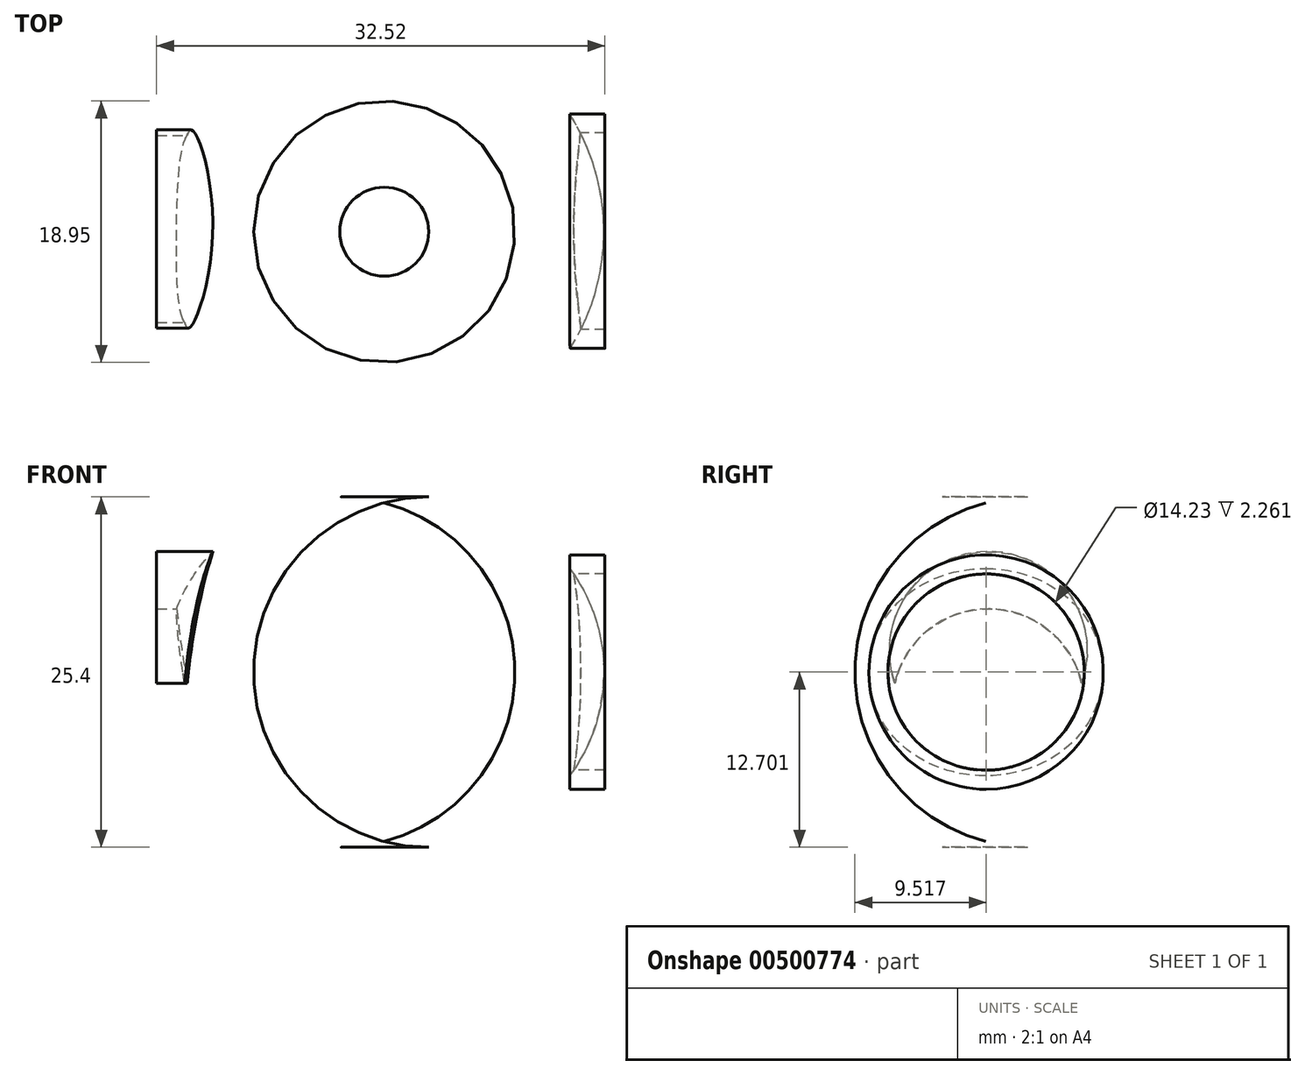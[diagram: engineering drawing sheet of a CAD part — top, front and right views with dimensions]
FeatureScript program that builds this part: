
annotation { "Feature Type Name" : "Feature", "Feature Type Description" : "" }
export const myFeature = defineFeature(function(context is Context, id is Id, definition is map)
    precondition{}
    {
        {
            var Q0;
            Q0=qCreatedBy(makeId("Top.planeOp"),FACE);
            var sketch = newSketch(context, id + "F0", { "sketchPlane" : qUnion([Q0])});
            skCircle(sketch, "E0", {"center": v(-45.47, 20) * mm, "radius": 15.93 * mm});
            skSolve(sketch);
        }
        {
            var Q0;
            Q0=makeQuery(id+"F0.imprint","IMPRINT",FACE,{"disambiguationData":[TD([[makeQuery(id+"F0.imprint","IMPRINT",EDGE,{"derivedFrom":sQuery(id+"F0.wireOp",EDGE,"E0")}),1.0]])]});
            extrude(context, id + "F1", {"entities" : qUnion([Q0]), "depth" : 25.4 * mm});
        }
        {
            var Q0;
            Q0=makeQuery(id+"F1.opExtrude","CAP_EDGE",EDGE,{"disambiguationData":[OSD([sQuery(id+"F0.wireOp",EDGE,"E0")])],"isStart":false});
            var Q1;
            Q1=makeQuery(id+"F1.opExtrude","CAP_EDGE",EDGE,{"disambiguationData":[OSD([sQuery(id+"F0.wireOp",EDGE,"E0")])],"isStart":true});
            fillet(context, id + "F2", {"entities" : qUnion([Q0, Q1]), "radius" : 12.7 * mm, "tangentPropagation" : true, "allowEdgeOverflow" : false});
        }
        {
            var Q0;
            Q0=qCreatedBy(makeId("Front.planeOp"),FACE);
            cPlane(context, id + "F3", {"entities" : qUnion([Q0]), "cplaneType" : CPlaneType.OFFSET, "offset" : 8.48 * mm, "oppositeDirection" : true, "width" : 152.4 * mm, "height" : 152.4 * mm});
        }
        {
            var Q0;
            Q0=qCreatedBy(id+"F3.planeOp",FACE);
            var sketch = newSketch(context, id + "F4", { "sketchPlane" : qUnion([Q0])});
            skCircle(sketch, "E1", {"center": v(-45.44, 12.7) * mm, "radius": 8 * mm});
            skFitSpline(sketch, "E2", {"points": [v(-42.57, 5.23) * mm, v(-44.89, 6.19) * mm, v(-47.41, 7.81) * mm, v(-49.76, 10.08) * mm, v(-50.28, 13.29) * mm, v(-49.38, 15.64) * mm, v(-47.11, 17.14) * mm, v(-44.37, 17.05) * mm, v(-42.02, 15.99) * mm, v(-41.12, 13.68) * mm, v(-41.85, 11.58) * mm, v(-44.29, 10.85) * mm, v(-46.64, 11.28) * mm, v(-47.5, 12.4) * mm, v(-47.33, 13.42) * mm, v(-45.44, 12.7) * mm, v(-44.07, 12.7) * mm, v(-42.75, 13.33) * mm, v(-42.88, 14.66) * mm, v(-43.52, 15.86) * mm, v(-45.1, 16.37) * mm, v(-47.2, 16.07) * mm, v(-48.65, 14.49) * mm, v(-49.04, 12.7) * mm, v(-48.44, 10.34) * mm, v(-46.55, 8.84) * mm, v(-44.16, 7.34) * mm, v(-41.85, 6.44) * mm, v(-40.86, 6.15) * mm, v(-42.57, 5.23) * mm]});
            skArc(sketch, "E3", {"start": v(-42.26, 6.54) * mm, "mid": v(-47.59, 19.27) * mm, "end": v(-44.4, 5.85) * mm});
            skPoint(sketch, "E4.17.internal.orphan", {"position": v(-45.56, 13.68) * mm});
            skPoint(sketch, "E4.19.internal.orphan", {"position": v(-45.44, 11.58) * mm});
            skPoint(sketch, "E4.21.internal.orphan", {"position": v(-43.51, 11.58) * mm});
            skPoint(sketch, "E4.24.internal.orphan", {"position": v(-42.87, 14.53) * mm});
            skFitSpline(sketch, "E5", {"points": [v(-47.1, 17.14) * mm, v(-45.98, 17.3) * mm, v(-44.76, 17.3) * mm, v(-43.5, 17.06) * mm, v(-42.6, 16.55) * mm, v(-41.92, 15.48) * mm, v(-41.67, 12.8) * mm, v(-42.25, 11.37) * mm, v(-42.91, 10.67) * mm, v(-44.73, 10.22) * mm, v(-45.97, 10.6) * mm, v(-46.64, 11.28) * mm, v(-47, 12.26) * mm, v(-46.88, 13.56) * mm, v(-46.14, 14.44) * mm, v(-45.69, 14.51) * mm, v(-45.4, 14.39) * mm, v(-45.56, 13.68) * mm, v(-45.81, 12.73) * mm, v(-45.44, 11.58) * mm, v(-44.41, 11.41) * mm, v(-43.51, 11.58) * mm, v(-43.04, 12.26) * mm, v(-42.75, 13.33) * mm, v(-42.87, 14.53) * mm, v(-42.87, 14.65) * mm, v(-43.51, 15.85) * mm, v(-45.1, 16.37) * mm, v(-46.09, 16.38) * mm, v(-47.2, 16.07) * mm, v(-47.1, 17.14) * mm]});
            skLineSegment(sketch, "E6", {"start": v(-45.98, 17.3) * mm, "end": v(-47.1, 17.14) * mm});
            skSolve(sketch);
        }
        {
            var Q0;
            Q0 = qSketchRegion(id + "F4", true);
            extrude(context, id + "F5", {"entities" : qUnion([Q0]), "operationType" : NewBodyOperationType.ADD, "depth" : 4.83 * mm});
        }
        {
            var Q0;
            Q0=qCreatedBy(makeId("Right.planeOp"),FACE);
            cPlane(context, id + "F6", {"entities" : qUnion([Q0]), "cplaneType" : CPlaneType.OFFSET, "offset" : 32 * mm, "oppositeDirection" : true, "width" : 152.4 * mm, "height" : 152.4 * mm});
        }
        {
            var Q0;
            Q0=qCreatedBy(id+"F6.planeOp",FACE);
            var sketch = newSketch(context, id + "F7", { "sketchPlane" : qUnion([Q0])});
            skCircle(sketch, "E7", {"center": v(20.04, 12.7) * mm, "radius": 8.5 * mm});
            skCircle(sketch, "E8", {"center": v(20.04, 12.7) * mm, "radius": 7.12 * mm});
            skSolve(sketch);
        }
        {
            var Q0;
            Q0=makeQuery(id+"F7.imprint","IMPRINT",FACE,{"disambiguationData":[TD([[makeQuery(id+"F7.imprint","IMPRINT",EDGE,{"derivedFrom":sQuery(id+"F7.wireOp",EDGE,"E7")}),1.0]])]});
            extrude(context, id + "F8", {"entities" : qUnion([Q0]), "operationType" : NewBodyOperationType.ADD, "depth" : 2.54 * mm});
        }
        {
            var Q0;
            Q0=qCreatedBy(makeId("Right.planeOp"),FACE);
            cPlane(context, id + "F9", {"entities" : qUnion([Q0]), "cplaneType" : CPlaneType.OFFSET, "offset" : 57.4 * mm, "oppositeDirection" : true, "width" : 152.4 * mm, "height" : 152.4 * mm});
        }
        {
            var Q0;
            Q0=qCreatedBy(id+"F9.planeOp",FACE);
            var sketch = newSketch(context, id + "F10", { "sketchPlane" : qUnion([Q0])});
            skArc(sketch, "E9", {"start": v(22.26, 7.39) * mm, "mid": v(24.68, 8.66) * mm, "end": v(26.45, 10.74) * mm});
            skArc(sketch, "E10", {"start": v(26.97, 11.88) * mm, "mid": v(20.2, 17.29) * mm, "end": v(13.42, 11.88) * mm});
            skLineSegment(sketch, "E11", {"start": v(22.26, 7.39) * mm, "end": v(22.26, 7.39) * mm});
            skLineSegment(sketch, "E12", {"start": v(18.16, 3.75) * mm, "end": v(18.16, 7.38) * mm});
            skLineSegment(sketch, "E13", {"start": v(22.26, 3.75) * mm, "end": v(18.16, 3.75) * mm});
            skLineSegment(sketch, "E14", {"start": v(22.26, 7.39) * mm, "end": v(22.26, 3.75) * mm});
            skLineSegment(sketch, "E15", {"start": v(18.16, 7.38) * mm, "end": v(18.16, 7.38) * mm});
            skArc(sketch, "E16", {"start": v(26.45, 10.74) * mm, "mid": v(20.2, 16.62) * mm, "end": v(13.94, 10.74) * mm});
            skArc(sketch, "E17.trimOffspring", {"start": v(26.97, 11.88) * mm, "mid": v(20.2, 21.44) * mm, "end": v(13.42, 11.88) * mm});
            skArc(sketch, "E18.trimOffspring", {"start": v(13.94, 10.74) * mm, "mid": v(15.72, 8.65) * mm, "end": v(18.16, 7.38) * mm});
            skSolve(sketch);
        }
        {
            var Q0;
            Q0 = qSketchRegion(id + "F10", true);
            extrude(context, id + "F11", {"entities" : qUnion([Q0]), "operationType" : NewBodyOperationType.ADD, "depth" : -4.57 * mm});
        }
    });
